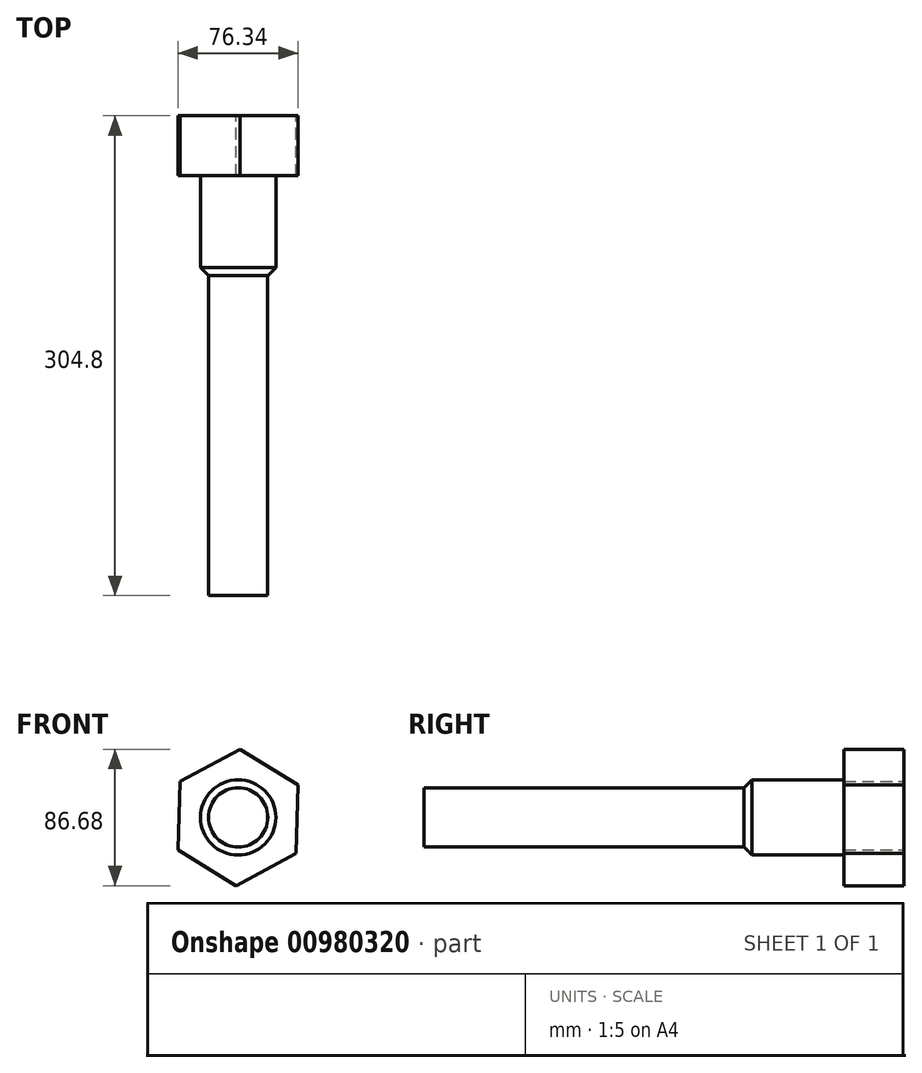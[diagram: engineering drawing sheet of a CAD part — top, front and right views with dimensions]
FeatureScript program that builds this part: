
annotation { "Feature Type Name" : "Feature", "Feature Type Description" : "" }
export const myFeature = defineFeature(function(context is Context, id is Id, definition is map)
    precondition{}
    {
        {
            var Q0;
            Q0=qCreatedBy(makeId("Front.planeOp"),FACE);
            var sketch = newSketch(context, id + "F0", { "sketchPlane" : qUnion([Q0])});
            skCircle(sketch, "E0.cCircle", {"center": v(0, 0) * mm, "radius": 37.55 * mm, "construction": true});
            skLineSegment(sketch, "E0.0", {"start": v(-36.89, 22.78) * mm, "end": v(1.28, 43.34) * mm});
            skLineSegment(sketch, "E0.1", {"start": v(1.28, 43.34) * mm, "end": v(38.17, 20.56) * mm});
            skLineSegment(sketch, "E0.2", {"start": v(38.17, 20.56) * mm, "end": v(36.89, -22.78) * mm});
            skLineSegment(sketch, "E0.3", {"start": v(36.89, -22.78) * mm, "end": v(-1.28, -43.34) * mm});
            skLineSegment(sketch, "E0.4", {"start": v(-1.28, -43.34) * mm, "end": v(-38.17, -20.56) * mm});
            skLineSegment(sketch, "E0.5", {"start": v(-38.17, -20.56) * mm, "end": v(-36.89, 22.78) * mm});
            skPoint(sketch, "E0.0.midPoint", {"position": v(-17.8, 33.06) * mm});
            skSolve(sketch);
        }
        {
            var Q0;
            Q0=makeQuery(id+"F0.imprint","IMPRINT",FACE,{"disambiguationData":[TD([[makeQuery(id+"F0.imprint","IMPRINT",EDGE,{"derivedFrom":sQuery(id+"F0.wireOp",EDGE,"E0.0")}),-1.0]])]});
            extrude(context, id + "F1", {"entities" : qUnion([Q0]), "depth" : 38.1 * mm, "offsetDistance" : 25.4 * mm});
        }
        {
            var Q0;
            Q0=makeQuery(id+"F1.opExtrude","CAP_FACE",FACE,{"disambiguationData":[OSD([sQuery(id+"F0.wireOp",EDGE,"E0.0"),sQuery(id+"F0.wireOp",EDGE,"E0.1"),sQuery(id+"F0.wireOp",EDGE,"E0.2"),sQuery(id+"F0.wireOp",EDGE,"E0.3"),sQuery(id+"F0.wireOp",EDGE,"E0.4"),sQuery(id+"F0.wireOp",EDGE,"E0.5")])],"isStart":false});
            var sketch = newSketch(context, id + "F2", { "sketchPlane" : qUnion([Q0])});
            skCircle(sketch, "E1", {"center": v(0, 0) * mm, "radius": 23.92 * mm});
            skSolve(sketch);
        }
        {
            var Q0;
            Q0 = qSketchRegion(id + "F2", true);
            extrude(context, id + "F3", {"entities" : qUnion([Q0]), "operationType" : NewBodyOperationType.ADD, "depth" : 63.5 * mm, "offsetDistance" : 25.4 * mm});
        }
        {
            var Q0;
            Q0=makeQuery(id+"F3.opExtrude","CAP_EDGE",EDGE,{"disambiguationData":[OSD([sQuery(id+"F2.wireOp",EDGE,"E1")])],"isStart":false});
            chamfer(context, id + "F4", {"entities" : qUnion([Q0]), "width" : 5.08 * mm, "tangentPropagation" : true});
        }
        {
            var Q0;
            Q0=makeQuery(id+"F3.opExtrude","CAP_FACE",FACE,{"disambiguationData":[OSD([sQuery(id+"F2.wireOp",EDGE,"E1")])],"isStart":false});
            var sketch = newSketch(context, id + "F5", { "sketchPlane" : qUnion([Q0])});
            skCircle(sketch, "E2", {"center": v(0, 0) * mm, "radius": 18.8 * mm});
            skSolve(sketch);
        }
        {
            var Q0;
            Q0 = qSketchRegion(id + "F5", true);
            extrude(context, id + "F6", {"entities" : qUnion([Q0]), "operationType" : NewBodyOperationType.ADD, "depth" : 203.2 * mm, "offsetDistance" : 25.4 * mm});
        }
    });
